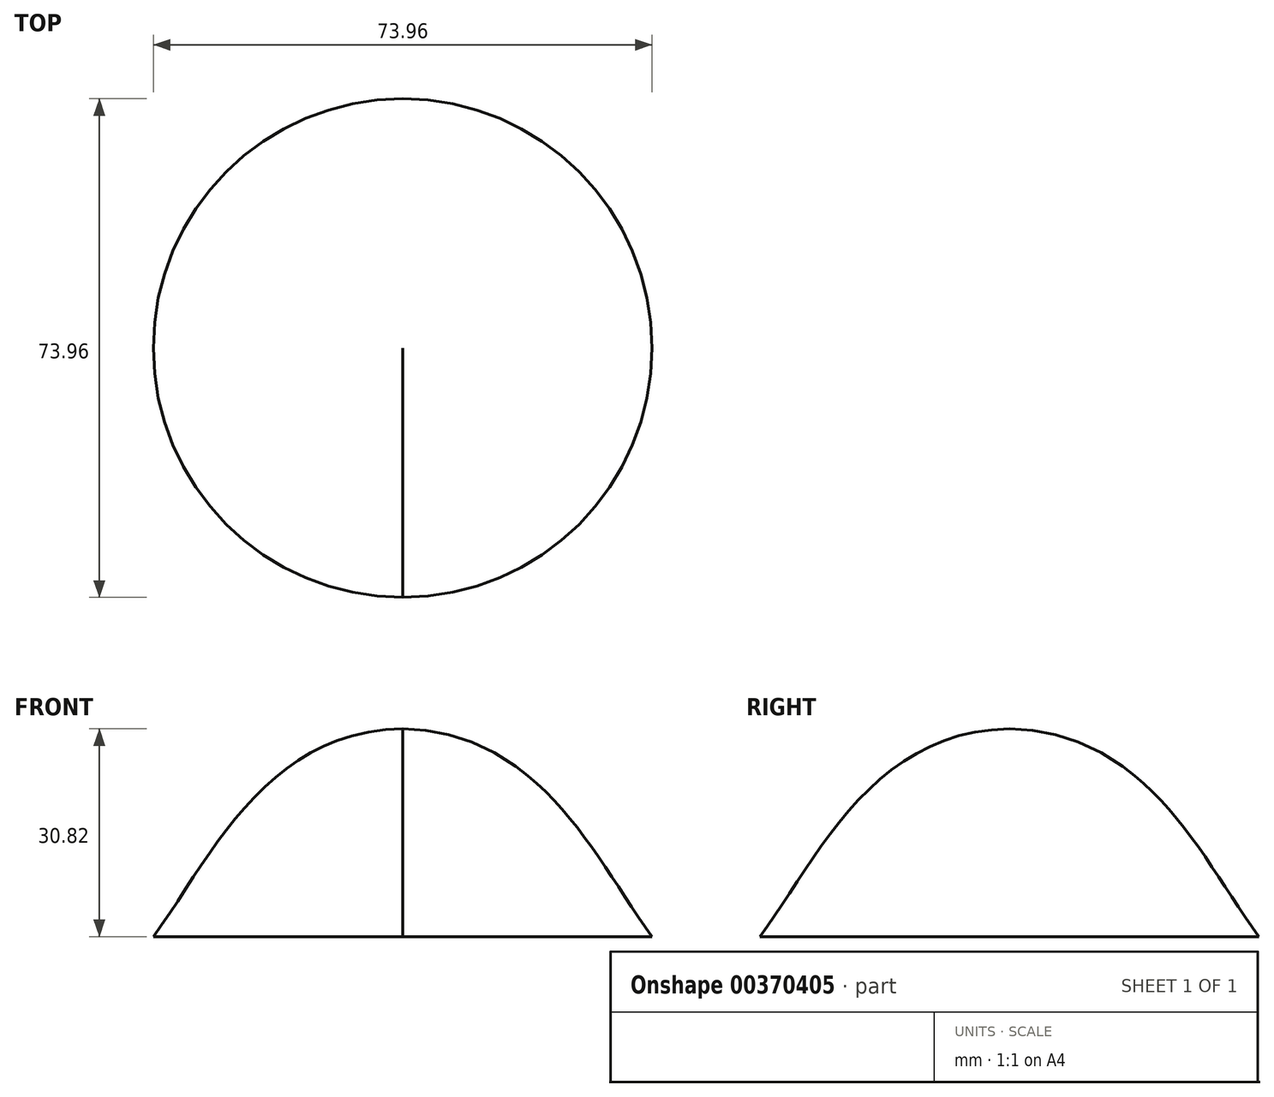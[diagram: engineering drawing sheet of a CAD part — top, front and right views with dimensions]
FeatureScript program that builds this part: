
annotation { "Feature Type Name" : "Feature", "Feature Type Description" : "" }
export const myFeature = defineFeature(function(context is Context, id is Id, definition is map)
    precondition{}
    {
        {
            var Q0;
            Q0=qCreatedBy(makeId("Right.planeOp"),FACE);
            var sketch = newSketch(context, id + "F0", { "sketchPlane" : qUnion([Q0])});
            skLineSegment(sketch, "E0", {"start": v(0, 0) * mm, "end": v(-36.98, 0) * mm});
            skLineSegment(sketch, "E1", {"start": v(0, 0) * mm, "end": v(0, 30.82) * mm});
            skFitSpline(sketch, "E2", {"points": [v(0, 30.82) * mm, v(-36.98, 0) * mm], "startDerivative": vector(-61.63, -0.82) * mm, "endDerivative": vector(-24.65, -33.28) * mm});
            skSolve(sketch);
        }
        {
            var Q0;
            Q0 = qSketchRegion(id + "F0", true);
            var Q1;
            Q1=sQuery(id+"F0.wireOp",EDGE,"E1");
            revolve(context, id + "F1", {"entities" : qUnion([Q0]), "axis" : qUnion([Q1]), "revolveType" : RevolveType.FULL});
        }
    });
